# Revit family: Arper_Aava-02_stool_bar_4woodlegs_upholstery_7640
name_source: partatom
category: Furniture
units: mm (PartAtom-declared; Revit-internal decimal feet)

## family parameters
Always vertical = Yes
Cut with Voids When Loaded = No
OmniClass Number = 23.40.20.00
OmniClass Title = General Furniture and Specialties
Room Calculation Point = No
Shared = No
Work Plane-Based = No

## types (1)
- Arper_Aava-02_stool_bar_4woodlegs_upholstery_7640
    Arper - Legs material = Arper - L0006
    Default Elevation = 0 mm  [stored 0 ft]
    Description = Stool on a 4-leg base in plywood with a reconstituted oak or walnut 
finish. Shell in wood upholstered with fabric, leather, coated fabric or 
customer’s own material. The upholstery can be separated and 
replaced by technical personnel, since it has been applied without 
the use of glue. Glides are also available, with felt insert for wood 
floors. Seat height 77 cm.
    Manufacturer = ARPER s.p.a.
    Model = Aava 02
    URL = http://www.arper.com

note: [stored X ft] marks values corroborated as IEEE doubles in the binary element streams (Revit-internal decimal feet)
